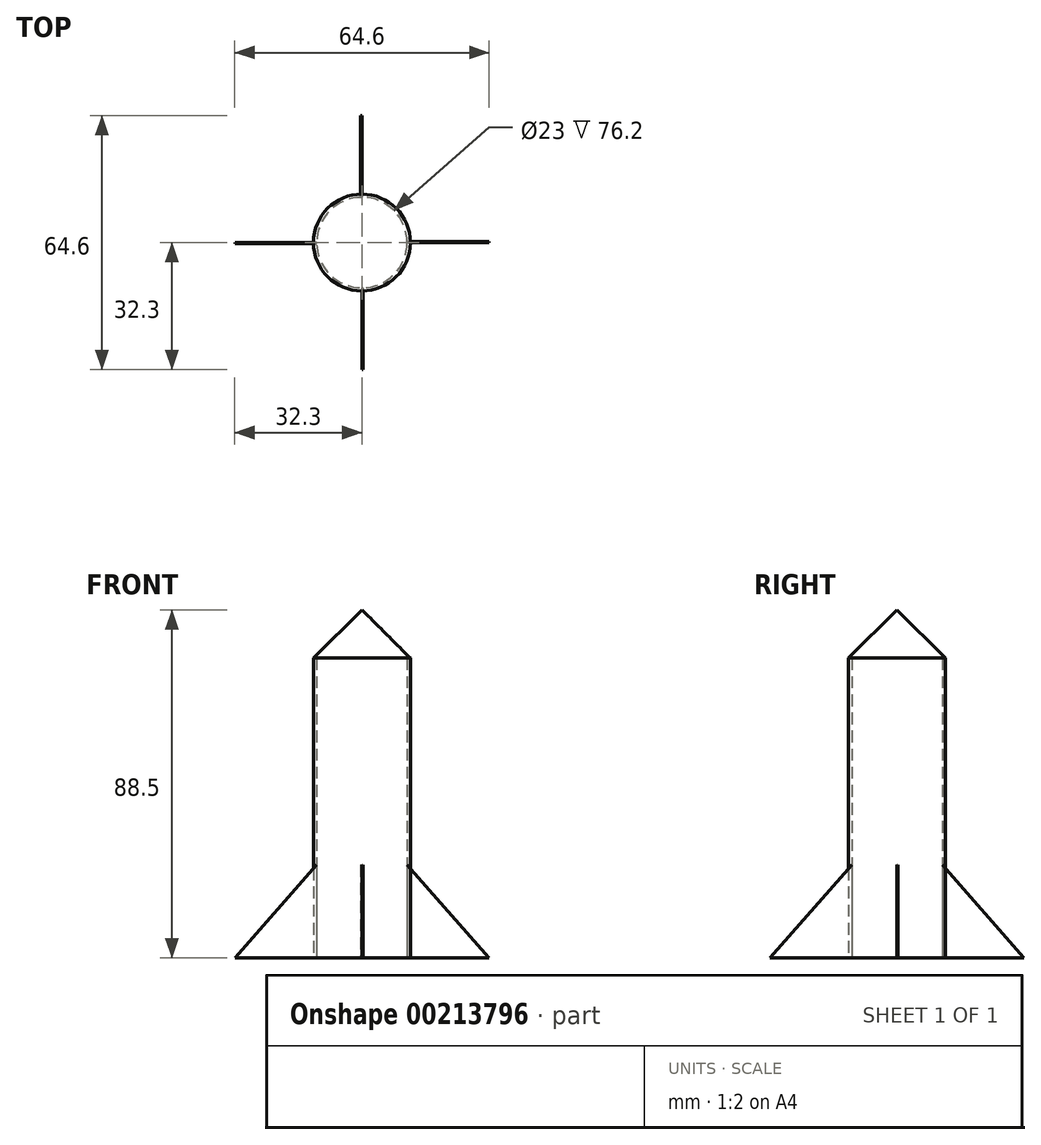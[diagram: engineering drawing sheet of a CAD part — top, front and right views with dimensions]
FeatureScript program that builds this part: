
annotation { "Feature Type Name" : "Feature", "Feature Type Description" : "" }
export const myFeature = defineFeature(function(context is Context, id is Id, definition is map)
    precondition{}
    {
        {
            var Q0;
            Q0=qCreatedBy(makeId("Top.planeOp"),FACE);
            var sketch = newSketch(context, id + "F0", { "sketchPlane" : qUnion([Q0])});
            skCircle(sketch, "E0", {"center": v(0, 0) * mm, "radius": 11.5 * mm});
            skCircle(sketch, "E1", {"center": v(0, 0) * mm, "radius": 12.3 * mm});
            skSolve(sketch);
        }
        {
            var Q0;
            Q0=makeQuery(id+"F0.imprint","IMPRINT",FACE,{"disambiguationData":[TD([[makeQuery(id+"F0.imprint","IMPRINT",EDGE,{"derivedFrom":sQuery(id+"F0.wireOp",EDGE,"E0")}),-1.0]])]});
            extrude(context, id + "F1", {"entities" : qUnion([Q0]), "depth" : 76.2 * mm});
        }
        {
            var Q0;
            Q0=makeQuery(id+"F1.opExtrude","CAP_FACE",FACE,{"disambiguationData":[OSD([sQuery(id+"F0.wireOp",EDGE,"E0"),sQuery(id+"F0.wireOp",EDGE,"E1")])],"isStart":false});
            var sketch = newSketch(context, id + "F2", { "sketchPlane" : qUnion([Q0])});
            skCircle(sketch, "E2.0", {"center": v(0, 0) * mm, "radius": 12.3 * mm});
            skSolve(sketch);
        }
        {
            var Q0;
            Q0 = qSketchRegion(id + "F2", true);
            extrude(context, id + "F3", {"entities" : qUnion([Q0]), "operationType" : NewBodyOperationType.ADD, "depth" : 50.8 * mm, "hasDraft" : true, "draftAngle" : 45 * degree, "draftPullDirection" : true});
        }
        {
            var Q0;
            Q0=qCreatedBy(makeId("Right.planeOp"),FACE);
            var sketch = newSketch(context, id + "F4", { "sketchPlane" : qUnion([Q0])});
            skLineSegment(sketch, "E3", {"start": v(-11.5, 0) * mm, "end": v(-32.3, 0) * mm});
            skLineSegment(sketch, "E4", {"start": v(-32.3, 0) * mm, "end": v(-11.5, 23.67) * mm});
            skLineSegment(sketch, "E5", {"start": v(-11.5, 23.67) * mm, "end": v(-11.5, 0) * mm});
            skSolve(sketch);
        }
        {
            var Q0;
            Q0=makeQuery(id+"F4.imprint","IMPRINT",FACE,{"disambiguationData":[TD([[makeQuery(id+"F4.imprint","IMPRINT",EDGE,{"derivedFrom":sQuery(id+"F4.wireOp",EDGE,"E3")}),-1.0]])]});
            extrude(context, id + "F5", {"entities" : qUnion([Q0]), "depth" : .3 * mm});
        }
        {
            var Q0;
            Q0=makeQuery(id+"F5.opExtrude","SWEPT_BODY",BODY,{"disambiguationData":[OSD([sQuery(id+"F4.wireOp",EDGE,"E3"),sQuery(id+"F4.wireOp",EDGE,"E4"),sQuery(id+"F4.wireOp",EDGE,"E5")])]});
            var Q1;
            Q1=sQuery(id+"F0.wireOp",EDGE,"E0");
            circularPattern(context, id + "F6", {"entities" : qUnion([Q0]), "axis" : qUnion([Q1]), "angle" : 360 * degree, "instanceCount" : 4, "equalSpace" : true});
        }
    });
